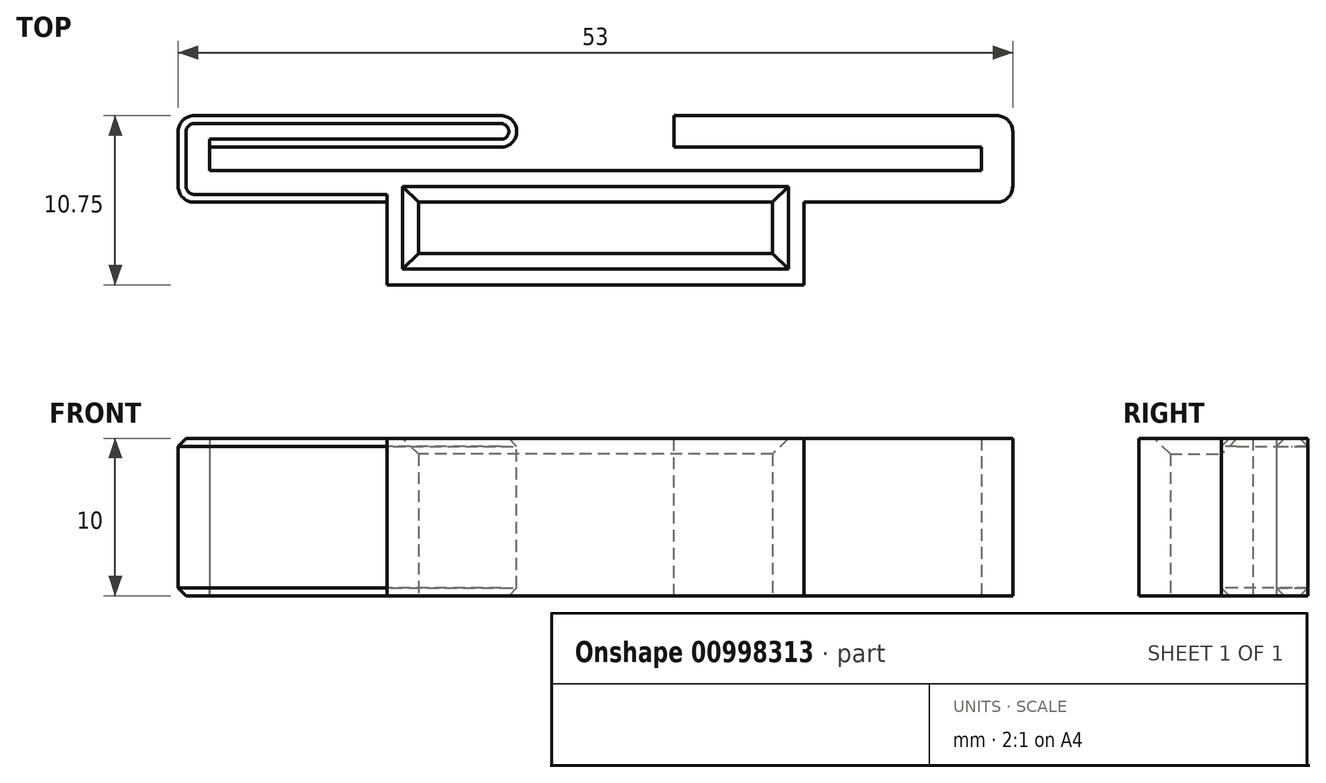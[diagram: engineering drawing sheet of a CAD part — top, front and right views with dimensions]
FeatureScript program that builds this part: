
annotation { "Feature Type Name" : "Feature", "Feature Type Description" : "" }
export const myFeature = defineFeature(function(context is Context, id is Id, definition is map)
    precondition{}
    {
        {
            var Q0;
            Q0=qCreatedBy(makeId("Top.planeOp"),FACE);
            var sketch = newSketch(context, id + "F0", { "sketchPlane" : qUnion([Q0])});
            skLineSegment(sketch, "E0.bottom", {"start": v(24.5, -0.75) * mm, "end": v(-24.5, -0.75) * mm});
            skLineSegment(sketch, "E0.top", {"start": v(24.5, 0.75) * mm, "end": v(-24.5, 0.75) * mm});
            skLineSegment(sketch, "E0.left", {"start": v(24.5, -0.75) * mm, "end": v(24.5, 0.75) * mm});
            skLineSegment(sketch, "E0.right", {"start": v(-24.5, -0.75) * mm, "end": v(-24.5, 0.75) * mm});
            skPoint(sketch, "E0.middle", {"position": v(0, 0) * mm});
            skLineSegment(sketch, "E1.bottom", {"start": v(26.5, -2.75) * mm, "end": v(-26.5, -2.75) * mm});
            skLineSegment(sketch, "E1.top", {"start": v(26.5, 2.75) * mm, "end": v(-26.5, 2.75) * mm});
            skLineSegment(sketch, "E1.left", {"start": v(26.5, -2.75) * mm, "end": v(26.5, 2.75) * mm});
            skLineSegment(sketch, "E1.right", {"start": v(-26.5, -2.75) * mm, "end": v(-26.5, 2.75) * mm});
            skSolve(sketch);
        }
        {
            var Q0;
            Q0=makeQuery(id+"F0.imprint","IMPRINT",FACE,{"disambiguationData":[TD([[makeQuery(id+"F0.imprint","IMPRINT",EDGE,{"derivedFrom":sQuery(id+"F0.wireOp",EDGE,"E0.bottom")}),1.0]])]});
            extrude(context, id + "F1", {"entities" : qUnion([Q0]), "endBound" : BoundingType.SYMMETRIC, "depth" : 10 * mm, "offsetDistance" : 25 * mm});
        }
        {
            var Q0;
            Q0=makeQuery(id+"F1.opExtrude","SWEPT_FACE",FACE,{"disambiguationData":[OSD([sQuery(id+"F0.wireOp",EDGE,"E1.top")])]});
            var sketch = newSketch(context, id + "F2", { "sketchPlane" : qUnion([Q0])});
            skLineSegment(sketch, "E2.bottom", {"start": v(5, -5) * mm, "end": v(-5, -5) * mm});
            skLineSegment(sketch, "E2.top", {"start": v(5, 5) * mm, "end": v(-5, 5) * mm});
            skLineSegment(sketch, "E2.left", {"start": v(5, -5) * mm, "end": v(5, 5) * mm});
            skLineSegment(sketch, "E2.right", {"start": v(-5, -5) * mm, "end": v(-5, 5) * mm});
            skPoint(sketch, "E2.middle", {"position": v(0, 0) * mm});
            skSolve(sketch);
        }
        {
            var Q0;
            Q0 = qSketchRegion(id + "F2", true);
            extrude(context, id + "F3", {"entities" : qUnion([Q0]), "operationType" : NewBodyOperationType.REMOVE, "endBound" : BoundingType.UP_TO_NEXT, "oppositeDirection" : true, "depth" : 25 * mm, "offsetDistance" : 25 * mm});
        }
        {
            var Q0;
            Q0=qCreatedBy(makeId("Top.planeOp"),FACE);
            var sketch = newSketch(context, id + "F4", { "sketchPlane" : qUnion([Q0])});
            skLineSegment(sketch, "E3.top", {"start": v(13.25, -8) * mm, "end": v(-13.25, -8) * mm});
            skLineSegment(sketch, "E3.left", {"start": v(13.25, -2.75) * mm, "end": v(13.25, -8) * mm});
            skLineSegment(sketch, "E3.right", {"start": v(-13.25, -2.75) * mm, "end": v(-13.25, -8) * mm});
            skPoint(sketch, "E3.middle", {"position": v(0, -5.38) * mm});
            skLineSegment(sketch, "E4.bottom", {"start": v(11.25, -6) * mm, "end": v(-11.25, -6) * mm});
            skLineSegment(sketch, "E4.left", {"start": v(11.25, -6) * mm, "end": v(11.25, -2.75) * mm});
            skLineSegment(sketch, "E4.right", {"start": v(-11.25, -6) * mm, "end": v(-11.25, -2.75) * mm});
            skPoint(sketch, "E4.middle", {"position": v(0, -4.37) * mm});
            skLineSegment(sketch, "E5", {"start": v(-13.25, -2.75) * mm, "end": v(-11.25, -2.75) * mm});
            skLineSegment(sketch, "E6", {"start": v(11.25, -2.75) * mm, "end": v(13.25, -2.75) * mm});
            skSolve(sketch);
        }
        {
            var Q0;
            Q0 = qSketchRegion(id + "F4", true);
            var Q1;
            Q1=makeQuery(id+"F1.opExtrude","CAP_FACE",FACE,{"disambiguationData":[OSD([sQuery(id+"F0.wireOp",EDGE,"E0.bottom"),sQuery(id+"F0.wireOp",EDGE,"E0.top"),sQuery(id+"F0.wireOp",EDGE,"E0.left"),sQuery(id+"F0.wireOp",EDGE,"E0.right"),sQuery(id+"F0.wireOp",EDGE,"E1.bottom"),sQuery(id+"F0.wireOp",EDGE,"E1.top"),sQuery(id+"F0.wireOp",EDGE,"E1.left"),sQuery(id+"F0.wireOp",EDGE,"E1.right")])],"isStart":false});
            var Q2;
            Q2=makeQuery(id+"F1.opExtrude","CAP_FACE",FACE,{"disambiguationData":[OSD([sQuery(id+"F0.wireOp",EDGE,"E0.bottom"),sQuery(id+"F0.wireOp",EDGE,"E0.top"),sQuery(id+"F0.wireOp",EDGE,"E0.left"),sQuery(id+"F0.wireOp",EDGE,"E0.right"),sQuery(id+"F0.wireOp",EDGE,"E1.bottom"),sQuery(id+"F0.wireOp",EDGE,"E1.top"),sQuery(id+"F0.wireOp",EDGE,"E1.left"),sQuery(id+"F0.wireOp",EDGE,"E1.right")])],"isStart":true});
            extrude(context, id + "F5", {"entities" : qUnion([Q0]), "operationType" : NewBodyOperationType.ADD, "endBound" : BoundingType.UP_TO_SURFACE, "depth" : 25 * mm, "endBoundEntityFace" : qUnion([Q1]), "offsetDistance" : 25 * mm, "hasSecondDirection" : true, "secondDirectionBound" : SecondDirectionBoundingType.UP_TO_SURFACE, "secondDirectionOppositeDirection" : true, "secondDirectionDepth" : 25 * mm, "secondDirectionBoundEntityFace" : qUnion([Q2])});
        }
        {
            var Q0;
            {var subQ0=sQuery(id+"F4.wireOp",EDGE,"E4.left");var subQ2=sQuery(id+"F0.wireOp",EDGE,"E1.bottom");Q0=makeQuery(id+"F5.boolean.opBoolean","SPLIT",EDGE,{"disambiguationData":[TD([makeQuery(id+"F5.opExtrude","SWEPT_FACE",FACE,{"disambiguationData":[OSD([subQ0])]})])],"derivedFrom":makeQuery(id+"F1.opExtrude","CAP_EDGE",EDGE,{"disambiguationData":[OSD([subQ2])],"isStart":false})});}
            var Q1;
            Q1=makeQuery(id+"F5.opExtrude","CAP_EDGE",EDGE,{"disambiguationData":[OSD([sQuery(id+"F4.wireOp",EDGE,"E4.bottom")])],"isStart":false});
            var Q2;
            Q2=makeQuery(id+"F5.opExtrude","CAP_EDGE",EDGE,{"disambiguationData":[OSD([sQuery(id+"F4.wireOp",EDGE,"E4.left")])],"isStart":false});
            var Q3;
            Q3=makeQuery(id+"F5.opExtrude","CAP_EDGE",EDGE,{"disambiguationData":[OSD([sQuery(id+"F4.wireOp",EDGE,"E4.right")])],"isStart":false});
            chamfer(context, id + "F6", {"entities" : qUnion([Q0, Q1, Q2, Q3]), "width" : 1 * mm, "tangentPropagation" : true});
        }
        {
            var Q0;
            Q0=makeQuery(id+"F3.boolean.opBoolean","COPY",EDGE,{"derivedFrom":makeQuery(id+"F3.opExtrude","CAP_EDGE",EDGE,{"disambiguationData":[OSD([sQuery(id+"F2.wireOp",EDGE,"E2.left")])],"isStart":true})});
            var Q1;
            Q1=makeQuery(id+"F3.boolean.opBoolean","COPY",EDGE,{"derivedFrom":makeQuery(id+"F3.opExtrude","CAP_EDGE",EDGE,{"disambiguationData":[OSD([sQuery(id+"F2.wireOp",EDGE,"E2.right")])],"isStart":false})});
            var Q2;
            Q2=makeQuery(id+"F3.boolean.opBoolean","COPY",EDGE,{"derivedFrom":makeQuery(id+"F3.opExtrude","CAP_EDGE",EDGE,{"disambiguationData":[OSD([sQuery(id+"F2.wireOp",EDGE,"E2.right")])],"isStart":true})});
            var Q3;
            Q3=makeQuery(id+"F3.boolean.opBoolean","COPY",EDGE,{"derivedFrom":makeQuery(id+"F3.opExtrude","CAP_EDGE",EDGE,{"disambiguationData":[OSD([sQuery(id+"F2.wireOp",EDGE,"E2.left")])],"isStart":false})});
            fillet(context, id + "F7", {"entities" : qUnion([Q0, Q1, Q2, Q3]), "radius" : 1 * mm, "tangentPropagation" : true, "allowEdgeOverflow" : false});
        }
        {
            var Q0;
            Q0=makeQuery(id+"F5.opExtrude","TWEAK_EDGE",EDGE,{"derivedFrom":[makeQuery(id+"F4.imprint","IMPRINT",EDGE,{"derivedFrom":sQuery(id+"F4.wireOp",EDGE,"E3.right")}),makeQuery(id+"F4.imprint","IMPRINT",EDGE,{"derivedFrom":sQuery(id+"F4.wireOp",EDGE,"E5")})]});
            var Q1;
            Q1=makeQuery(id+"F1.opExtrude","SWEPT_EDGE",EDGE,{"disambiguationData":[OSD([sQuery(id+"F0.wireOp",EDGE,"E1.bottom"),sQuery(id+"F0.wireOp",EDGE,"E1.right")])]});
            var Q2;
            Q2=makeQuery(id+"F1.opExtrude","SWEPT_EDGE",EDGE,{"disambiguationData":[OSD([sQuery(id+"F0.wireOp",EDGE,"E1.bottom"),sQuery(id+"F0.wireOp",EDGE,"E1.left")])]});
            var Q3;
            Q3=makeQuery(id+"F5.opExtrude","TWEAK_EDGE",EDGE,{"derivedFrom":[makeQuery(id+"F4.imprint","IMPRINT",EDGE,{"derivedFrom":sQuery(id+"F4.wireOp",EDGE,"E3.top")}),makeQuery(id+"F4.imprint","IMPRINT",EDGE,{"derivedFrom":sQuery(id+"F4.wireOp",EDGE,"E3.right")})]});
            var Q4;
            Q4=makeQuery(id+"F1.opExtrude","SWEPT_EDGE",EDGE,{"disambiguationData":[OSD([sQuery(id+"F0.wireOp",EDGE,"E1.top"),sQuery(id+"F0.wireOp",EDGE,"E1.left")])]});
            var Q5;
            Q5=makeQuery(id+"F5.opExtrude","TWEAK_EDGE",EDGE,{"derivedFrom":[makeQuery(id+"F4.imprint","IMPRINT",EDGE,{"derivedFrom":sQuery(id+"F4.wireOp",EDGE,"E3.top")}),makeQuery(id+"F4.imprint","IMPRINT",EDGE,{"derivedFrom":sQuery(id+"F4.wireOp",EDGE,"E3.left")})]});
            var Q6;
            Q6=makeQuery(id+"F5.opExtrude","TWEAK_EDGE",EDGE,{"derivedFrom":[makeQuery(id+"F4.imprint","IMPRINT",EDGE,{"derivedFrom":sQuery(id+"F4.wireOp",EDGE,"E3.left")}),makeQuery(id+"F4.imprint","IMPRINT",EDGE,{"derivedFrom":sQuery(id+"F4.wireOp",EDGE,"E6")})]});
            var Q7;
            Q7=makeQuery(id+"F1.opExtrude","SWEPT_EDGE",EDGE,{"disambiguationData":[OSD([sQuery(id+"F0.wireOp",EDGE,"E1.top"),sQuery(id+"F0.wireOp",EDGE,"E1.right")])]});
            fillet(context, id + "F8", {"entities" : qUnion([Q0, Q1, Q2, Q3, Q4, Q5, Q6, Q7]), "radius" : 1 * mm, "tangentPropagation" : true, "allowEdgeOverflow" : false});
        }
        {
            var Q0;
            {var subQ0=sQuery(id+"F0.wireOp",EDGE,"E1.right");var subQ1=sQuery(id+"F0.wireOp",EDGE,"E1.top");Q0=makeQuery(id+"F3.boolean.opBoolean","SPLIT",EDGE,{"disambiguationData":[TD([makeQuery(id+"F1.opExtrude","SWEPT_FACE",FACE,{"disambiguationData":[OSD([subQ0])]})])],"derivedFrom":makeQuery(id+"F1.opExtrude","CAP_EDGE",EDGE,{"disambiguationData":[OSD([subQ1])],"isStart":true})});}
            var Q1;
            {var subQ0=sQuery(id+"F0.wireOp",EDGE,"E1.right");var subQ1=sQuery(id+"F0.wireOp",EDGE,"E1.top");Q1=makeQuery(id+"F3.boolean.opBoolean","SPLIT",EDGE,{"disambiguationData":[TD([makeQuery(id+"F1.opExtrude","SWEPT_FACE",FACE,{"disambiguationData":[OSD([subQ0])]})])],"derivedFrom":makeQuery(id+"F1.opExtrude","CAP_EDGE",EDGE,{"disambiguationData":[OSD([subQ1])],"isStart":false})});}
            chamfer(context, id + "F9", {"entities" : qUnion([Q0, Q1]), "width" : 0.5 * mm, "tangentPropagation" : true});
        }
    });
